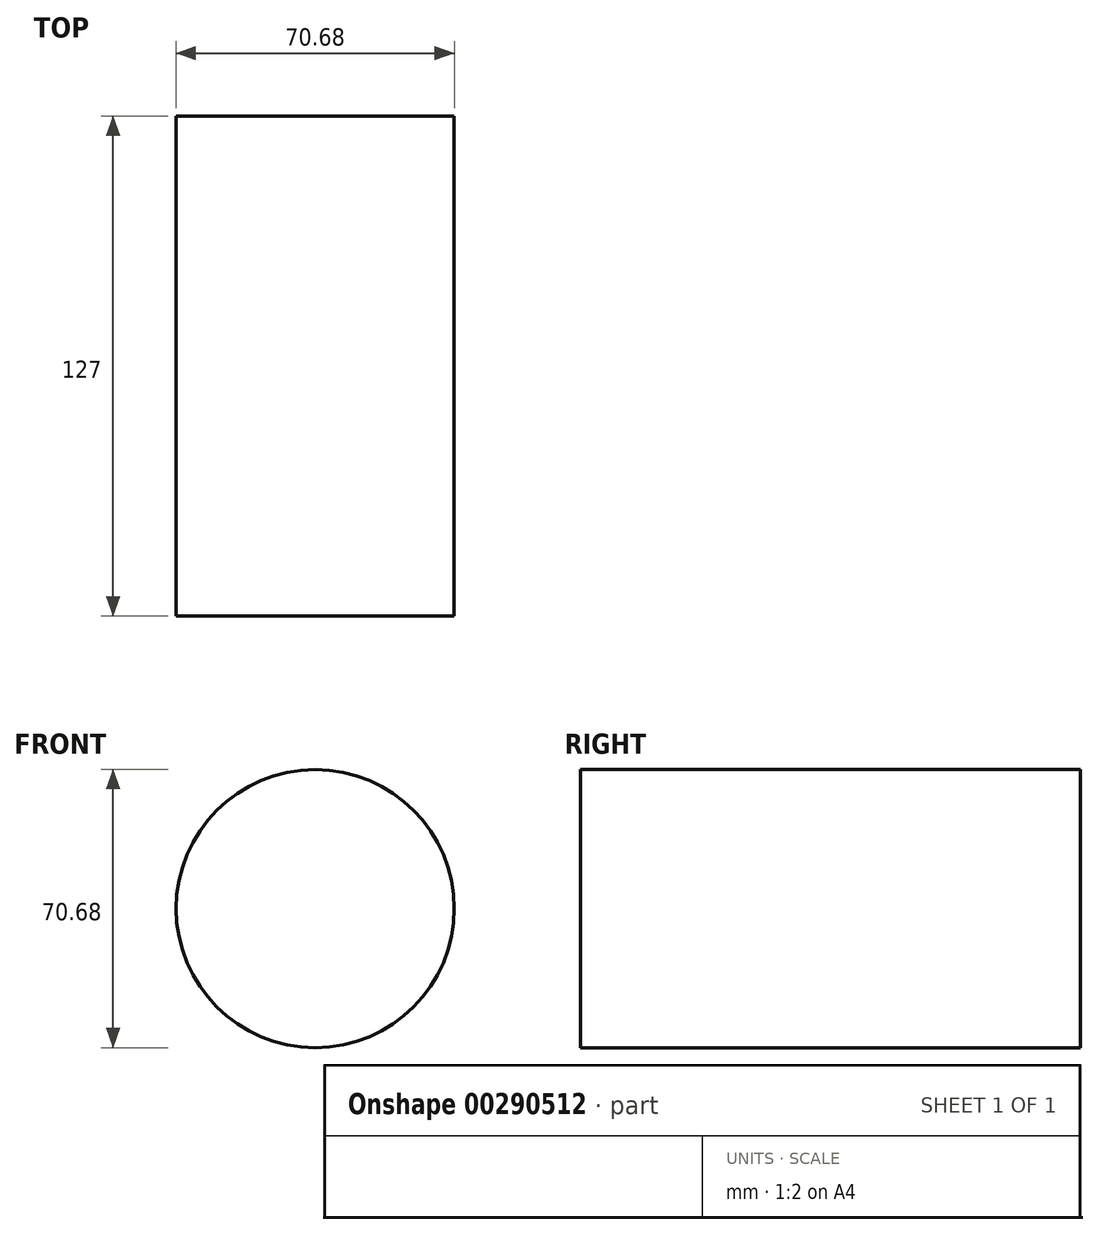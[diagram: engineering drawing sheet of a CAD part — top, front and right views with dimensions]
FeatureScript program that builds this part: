
annotation { "Feature Type Name" : "Feature", "Feature Type Description" : "" }
export const myFeature = defineFeature(function(context is Context, id is Id, definition is map)
    precondition{}
    {
        {
            var Q0;
            Q0=qCreatedBy(makeId("Front.planeOp"),FACE);
            var sketch = newSketch(context, id + "F0", { "sketchPlane" : qUnion([Q0])});
            skCircle(sketch, "E0", {"center": v(0, 0) * mm, "radius": 35.34 * mm});
            skSolve(sketch);
        }
        {
            var Q0;
            Q0=makeQuery(id+"F0.imprint","IMPRINT",FACE,{"disambiguationData":[TD([[makeQuery(id+"F0.imprint","IMPRINT",EDGE,{"derivedFrom":sQuery(id+"F0.wireOp",EDGE,"E0")}),1.0]])]});
            extrude(context, id + "F1", {"entities" : qUnion([Q0]), "endBound" : BoundingType.SYMMETRIC, "depth" : 127 * mm});
        }
    });
